# Revit family: SUBACUATICA_SLNSA.RGB
name_source: partatom
category: Luminarias
units: mm (PartAtom-declared; Revit-internal decimal feet)

## family parameters
Compartido = No
Corte con vacíos al cargar = No
Cota de conector redondo = Diámetro de uso
Origen de luz = Sí
Punto de cálculo de habitación = No
Se basa en plano de trabajo = Sí
Siempre vertical = No
Tipo de pieza = Normal

## types (1)
- SUBACUATICA_SLNSA.RGB
    Cambio de temperatura de color de luz atenuada = <Ninguno>
    Comentarios de vataje = 24V
    Descripción = TIRA LED SUBACUATICA HECHA DE SILICON CON UNA POTENCIA DE 5W/M, USO PARA EXTERIORES O ALBERCAS IP68, IRC 80, TEMPERATURA EN RGB, 144 LED´S/M, PRESENTACION DE 15M Y LOS CORTES DEBEN DE SER SOLICITADOS DESDE ORIGEN PARA GARANTIZAR EL SELLADO (DESDE 2.5CM), PROFUNDAID MAXIMA DE 2M, RESISTENTE A SOLUCIONES SALINAS, A CLORO, FUEGO Y RAYOS UV. ALIMENTADO A 24V, REQUIERE ACCESORIOS.
    Elevación por defecto = 0 mm  [stored 0 ft]
    Fabricante = BRILLANT
    Filtro de color = 16777215
    Longitud de línea de emisión = 600 mm
    Lámpara = 3838 SMD
    Marca = BRILLANT
    Modelo = SLNSA.RGB
    Tamaño de símbolo de origen de luz = 610 mm

note: [stored X ft] marks values corroborated as IEEE doubles in the binary element streams (Revit-internal decimal feet)

## geometry (parser evidence)
native form markers: Blend x2
no freeform markers — native parametric forms only
